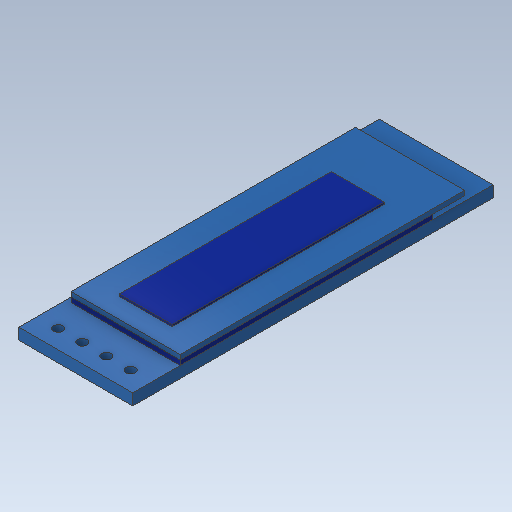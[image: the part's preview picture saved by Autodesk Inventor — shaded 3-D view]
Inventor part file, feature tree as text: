
AUTODESK INVENTOR PART (.ipt)
format: ipt  version: 2020.1 (Build 241239000, 239)  size: 267,264 bytes
history: native  units: mm
features: extrude x7, sketch x5, fillet x1, plane x1
ambient origin geometry x8: Origin, YZ Plane, XZ Plane, XY Plane, X Axis, Y Axis, Z Axis, Center Point
bodies: Solid1 (feature_tree), Solid2 (feature_tree)
feature tree (14):
  sketch  "Sketch1"  dims[d0=12.0mm d1=38.0mm]
  extrude  "Extrusion1"  Depth=38.0mm
  extrude  "Extrusion2"  Depth=30.0mm
  sketch  "Sketch2"  dims[d2=3.0mm d3=30.0mm]
  extrude  "Extrusion3"  Depth=7.58mm
  extrude  "Extrusion4"  Depth=5.58mm
  extrude  "Extrusion5"  Depth=1.96mm
  fillet  "Fillet1"  Radius=7.51mm
  extrude  "Extrusion6"  Depth=2.4mm
  plane  "Work Plane2"
  extrude  "Extrusion7"  Depth=1.96mm
  sketch  "Sketch3"  dims[d5=26.6mm d6=7.58mm]
  sketch  "Sketch4"  dims[d7=24.38mm d8=5.58mm]
  sketch  "Sketch5"  dims[d9=22.38mm d10=1.96mm d11=7.51mm d13=2.19mm d14=1.96mm d15=1.0mm d16=40.0mm d18=2.54mm d19=10.0mm d21=10.0mm d23=1.2mm d24=0.0mm d25=0.5mm d26=0.0mm d27=1.0mm d28=1.2mm d29=0.5mm d30=0.0mm d32=0.001mm d33=0.001mm d34=0.001mm d35=11.5mm d36=0.001mm d37=0.2mm d38=0.0mm d39=0.5mm d40=0.0mm d41=1.0mm d43=2.05mm d46=1.89mm d47=0.282843mm d48=45.0deg d49=0.6mm d50=0.6mm d51=2.4mm d52=0.0mm d53=135.0deg d54=135.0deg d55=135.0deg d56=2.05mm d57=1.89mm d58=0.282843mm d59=45.0deg d60=0.6mm d61=0.6mm d62=135.0deg d63=135.0deg d64=135.0deg d65=2.05mm d66=1.89mm d67=0.282843mm d68=45.0deg d69=0.6mm d70=0.6mm d71=135.0deg d72=135.0deg d73=135.0deg d74=2.05mm d75=1.89mm d76=0.282843mm d77=45.0deg d78=0.6mm d79=0.6mm d80=135.0deg d81=135.0deg d82=135.0deg d85=11.0mm d86=0.0mm d87=1.4mm]
